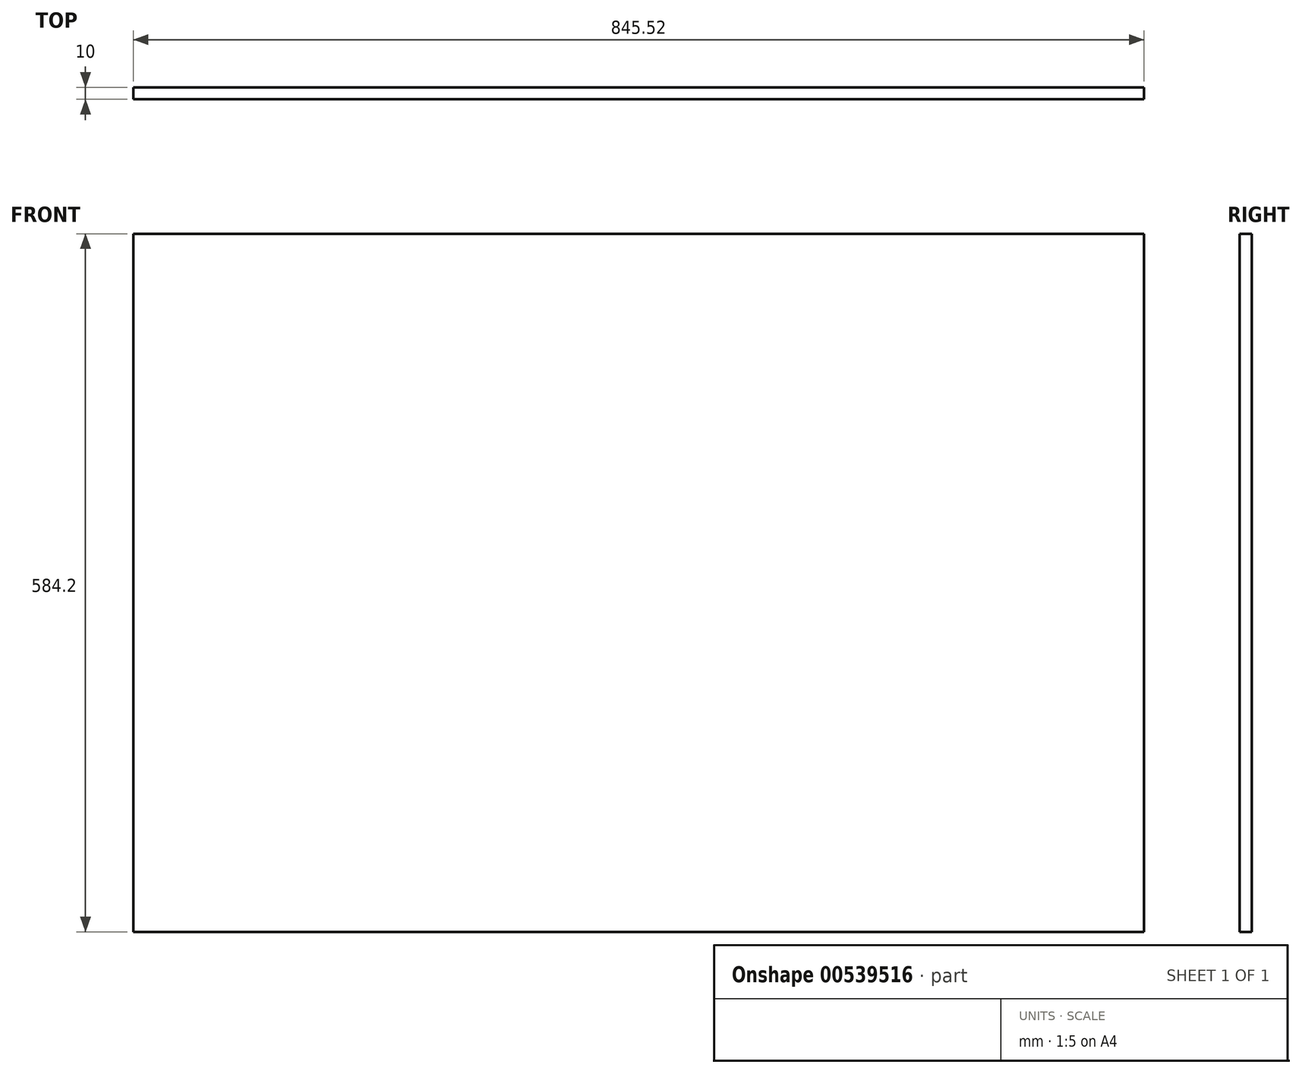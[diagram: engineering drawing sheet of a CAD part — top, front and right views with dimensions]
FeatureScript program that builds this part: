
annotation { "Feature Type Name" : "Feature", "Feature Type Description" : "" }
export const myFeature = defineFeature(function(context is Context, id is Id, definition is map)
    precondition{}
    {
        {
            var Q0;
            Q0=qCreatedBy(makeId("Front.planeOp"),FACE);
            var sketch = newSketch(context, id + "F0", { "sketchPlane" : qUnion([Q0])});
            skLineSegment(sketch, "E0.bottom", {"start": v(422.76, -292.1) * mm, "end": v(-422.76, -292.1) * mm});
            skLineSegment(sketch, "E0.top", {"start": v(422.76, 292.1) * mm, "end": v(-422.76, 292.1) * mm});
            skLineSegment(sketch, "E0.left", {"start": v(422.76, -292.1) * mm, "end": v(422.76, 292.1) * mm});
            skLineSegment(sketch, "E0.right", {"start": v(-422.76, -292.1) * mm, "end": v(-422.76, 292.1) * mm});
            skPoint(sketch, "E0.middle", {"position": v(0, 0) * mm});
            skSolve(sketch);
        }
        {
            var Q0;
            Q0=makeQuery(id+"F0.imprint","IMPRINT",FACE,{"disambiguationData":[TD([[makeQuery(id+"F0.imprint","IMPRINT",EDGE,{"derivedFrom":sQuery(id+"F0.wireOp",EDGE,"E0.bottom")}),-1.0]])]});
            extrude(context, id + "F1", {"entities" : qUnion([Q0]), "depth" : 10 * mm});
        }
    });
